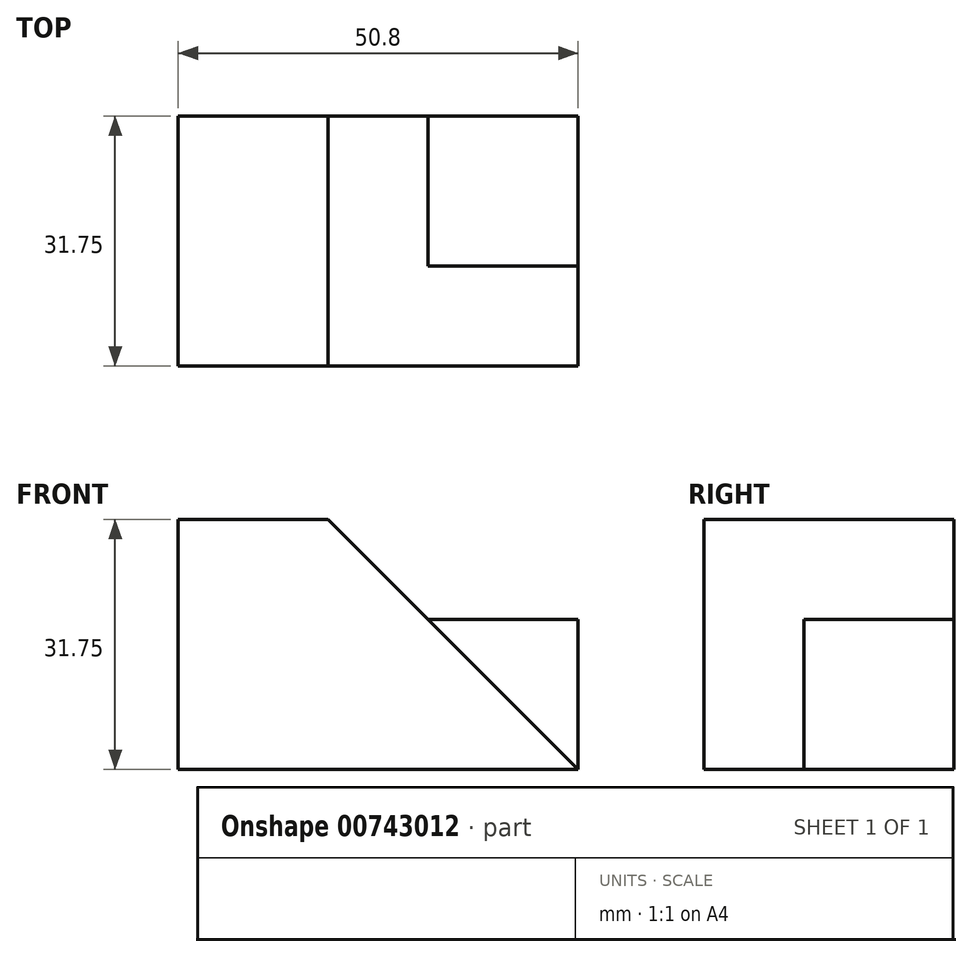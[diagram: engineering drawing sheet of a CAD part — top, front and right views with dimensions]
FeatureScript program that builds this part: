
annotation { "Feature Type Name" : "Feature", "Feature Type Description" : "" }
export const myFeature = defineFeature(function(context is Context, id is Id, definition is map)
    precondition{}
    {
        {
            var Q0;
            Q0=qCreatedBy(makeId("Front.planeOp"),FACE);
            var sketch = newSketch(context, id + "F0", { "sketchPlane" : qUnion([Q0])});
            skLineSegment(sketch, "E0", {"start": v(0, 0) * mm, "end": v(0, 31.75) * mm});
            skLineSegment(sketch, "E1", {"start": v(0, 31.75) * mm, "end": v(50.8, 31.75) * mm});
            skLineSegment(sketch, "E2", {"start": v(50.8, 31.75) * mm, "end": v(50.8, 0) * mm});
            skLineSegment(sketch, "E3", {"start": v(50.8, 0) * mm, "end": v(0, 0) * mm});
            skSolve(sketch);
        }
        {
            var Q0;
            Q0=makeQuery(id+"F0.imprint","IMPRINT",FACE,{"disambiguationData":[TD([[makeQuery(id+"F0.imprint","IMPRINT",EDGE,{"derivedFrom":sQuery(id+"F0.wireOp",EDGE,"E0")}),-1.0]])]});
            extrude(context, id + "F1", {"entities" : qUnion([Q0]), "depth" : 31.75 * mm, "offsetDistance" : 25.4 * mm});
        }
        {
            var Q0;
            Q0=makeQuery(id+"F1.opExtrude","CAP_FACE",FACE,{"disambiguationData":[OSD([sQuery(id+"F0.wireOp",EDGE,"E0"),sQuery(id+"F0.wireOp",EDGE,"E1"),sQuery(id+"F0.wireOp",EDGE,"E2"),sQuery(id+"F0.wireOp",EDGE,"E3")])],"isStart":false});
            var sketch = newSketch(context, id + "F2", { "sketchPlane" : qUnion([Q0])});
            skLineSegment(sketch, "E4", {"start": v(50.8, 0) * mm, "end": v(19.05, 31.75) * mm});
            skLineSegment(sketch, "E5", {"start": v(19.05, 31.75) * mm, "end": v(50.8, 31.75) * mm});
            skLineSegment(sketch, "E6", {"start": v(50.8, 31.75) * mm, "end": v(50.8, 0) * mm});
            skSolve(sketch);
        }
        {
            var Q0;
            Q0=makeQuery(id+"F2.imprint","IMPRINT",FACE,{"disambiguationData":[TD([[makeQuery(id+"F2.imprint","IMPRINT",EDGE,{"derivedFrom":sQuery(id+"F2.wireOp",EDGE,"E4")}),-1.0]])]});
            extrude(context, id + "F3", {"entities" : qUnion([Q0]), "operationType" : NewBodyOperationType.REMOVE, "oppositeDirection" : true, "depth" : 31.75 * mm, "offsetDistance" : 25.4 * mm});
        }
        {
            var Q0;
            Q0=makeQuery(id+"F1.opExtrude","CAP_FACE",FACE,{"disambiguationData":[OSD([sQuery(id+"F0.wireOp",EDGE,"E0"),sQuery(id+"F0.wireOp",EDGE,"E1"),sQuery(id+"F0.wireOp",EDGE,"E2"),sQuery(id+"F0.wireOp",EDGE,"E3")])],"isStart":true});
            var sketch = newSketch(context, id + "F4", { "sketchPlane" : qUnion([Q0])});
            skLineSegment(sketch, "E7", {"start": v(-50.8, 0) * mm, "end": v(-50.8, 19.05) * mm});
            skLineSegment(sketch, "E8", {"start": v(-50.8, 19.05) * mm, "end": v(-31.75, 19.05) * mm});
            skLineSegment(sketch, "E9", {"start": v(-31.75, 19.05) * mm, "end": v(-50.8, 0) * mm});
            skSolve(sketch);
        }
        {
            var Q0;
            Q0=makeQuery(id+"F4.imprint","IMPRINT",FACE,{"disambiguationData":[TD([[makeQuery(id+"F4.imprint","IMPRINT",EDGE,{"derivedFrom":sQuery(id+"F4.wireOp",EDGE,"E7")}),-1.0]])]});
            extrude(context, id + "F5", {"entities" : qUnion([Q0]), "operationType" : NewBodyOperationType.ADD, "oppositeDirection" : true, "depth" : 19.05 * mm, "offsetDistance" : 25.4 * mm});
        }
    });
